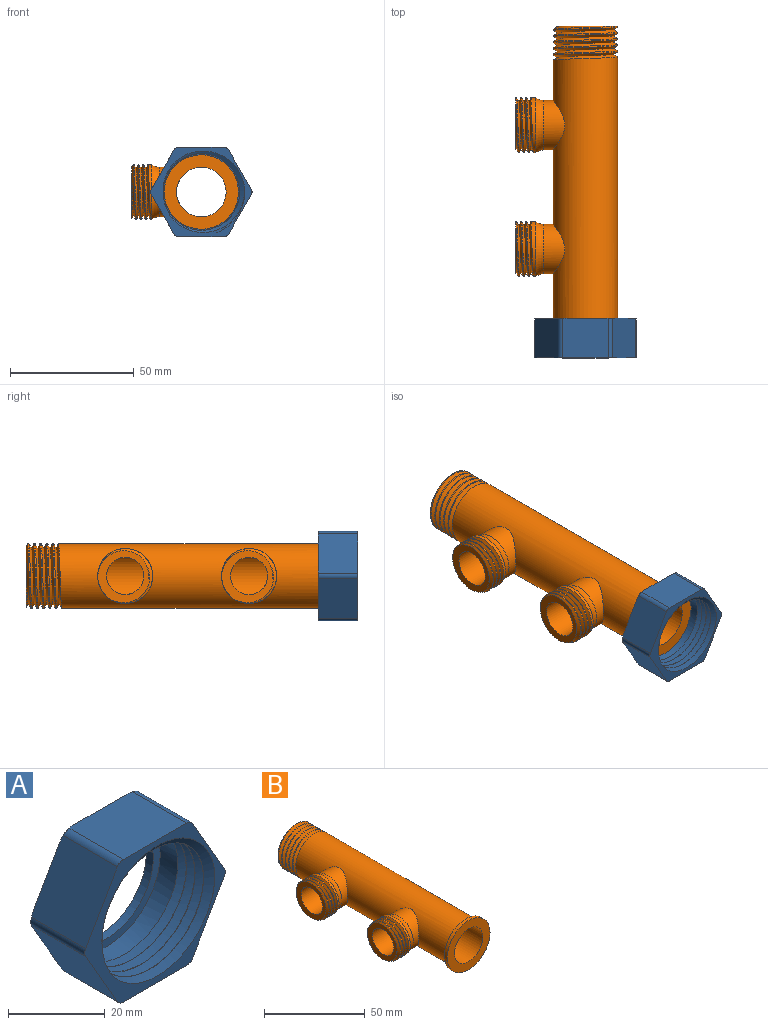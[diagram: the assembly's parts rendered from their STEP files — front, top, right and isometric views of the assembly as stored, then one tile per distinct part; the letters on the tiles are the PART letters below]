
ASSEMBLY  parts=2 mates=1
PART A: 29 faces, bbox 43.9x19.3x42.2 mm
  f0: cylinder r=15.45mm len=30.9mm, axis (0,1,0), area 510.3mm2, adj f3,f10,f26,f27,f28
  f1: cylinder r=15.45mm len=19.43mm, axis (0,1,0), area 2.6mm2, adj f2,f4,f27,f28
  f2: cylinder r=15.45mm len=30.9mm, axis (0,1,0), area 9.7mm2, adj f1,f3,f27,f28
  f3: cylinder r=15.45mm len=30.9mm, axis (0,1,0), area 9.7mm2, adj f0,f2,f27,f28
  f4: plane 42.7x37.75mm, normal (0,-1,0), area 270mm2, adj f1,f14,f15,f16,f17,f18,f19,f20
  f5: torus R=19.45mm, axis (0,1,0), area 3.3mm2, adj f12,f14,f15,f20
  f6: torus R=19.45mm, axis (0,1,0), area 3.3mm2, adj f12,f15,f16,f21
  f7: torus R=19.45mm, axis (0,1,0), area 3.3mm2, adj f12,f16,f17,f22
  f8: torus R=19.45mm, axis (0,1,0), area 3.3mm2, adj f12,f17,f18,f23
  f9: torus R=19.45mm, axis (0,1,0), area 3.3mm2, adj f12,f14,f19,f25
  f10: plane 30.9x30.9mm, normal (0,-1,0), area 179.6mm2, adj f0,f13
  f11: torus R=19.45mm, axis (0,1,0), area 3.3mm2, adj f12,f18,f19,f24
  f12: plane 38.9x36mm, normal (0,1,0), area 532mm2, adj f5,f6,f7,f8,f9,f11,f13,f14
  f13: cylinder r=13.47mm len=26.95mm, axis (0,1,0), area 175.1mm2, adj f10,f12
  f14: plane 16.07x16.07mm, normal (-0.87,0,-0.5), area 295.4mm2, adj f4,f5,f9,f12,f20,f25
  f15: plane 16.07x16.07mm, normal (-0.87,0,0.5), area 295.4mm2, adj f4,f5,f6,f12,f20,f21
  f16: plane 18.54x16.07mm, normal (0,0,1), area 295.4mm2, adj f4,f6,f7,f12,f21,f22
  f17: plane 16.07x16.07mm, normal (0.87,0,0.5), area 295.4mm2, adj f4,f7,f8,f12,f22,f23
  f18: plane 16.07x16.07mm, normal (0.87,0,-0.5), area 295.4mm2, adj f4,f8,f11,f12,f23,f24
  f19: plane 18.54x16.07mm, normal (0,0,-1), area 295.4mm2, adj f4,f9,f11,f12,f24,f25
  f20: cylinder r=2mm len=15.84mm, axis (0,-1,0), area 33.2mm2, adj f4,f5,f14,f15
  f21: cylinder r=2mm len=15.84mm, axis (0,-1,0), area 33.2mm2, adj f4,f6,f15,f16
  f22: cylinder r=2mm len=15.84mm, axis (0,-1,0), area 33.2mm2, adj f4,f7,f16,f17
  f23: cylinder r=2mm len=15.84mm, axis (0,-1,0), area 33.2mm2, adj f4,f8,f17,f18
  f24: cylinder r=2mm len=15.84mm, axis (0,-1,0), area 33.2mm2, adj f4,f11,f18,f19
  f25: cylinder r=2mm len=15.84mm, axis (0,-1,0), area 33.2mm2, adj f4,f9,f14,f19
  f26: plane 2.4x2.08mm, normal (0,0,-1), area 2.5mm2, adj f0,f27,f28
  f27: bspline ~40.48x35.06mm, area 934.5mm2, adj f0,f1,f2,f3,f4,f26,f28
  f28: bspline ~40.48x35.06mm, area 817.6mm2, adj f0,f1,f2,f3,f4,f26,f27
PART B: 31 faces, bbox 45.2x124.3x31.2 mm
  f0: cylinder r=10mm len=122mm, axis (0,1,0), area 7279.5mm2, adj f8,f16,f24,f26
  f1: cylinder r=13mm len=107.5mm, axis (0,1,0), area 7987.8mm2, adj f7,f15,f23,f27,f29,f30
  f2: cylinder r=13mm len=12.4mm, axis (0,1,0), area 4.1mm2, adj f3,f8,f28
  f3: cylinder r=13mm len=26mm, axis (0,1,0), area 40.9mm2, adj f2,f4,f28,f29
  f4: cylinder r=13mm len=26mm, axis (0,1,0), area 40.8mm2, adj f3,f5,f28,f29
  f5: cylinder r=13mm len=26mm, axis (0,1,0), area 40.9mm2, adj f4,f6,f28,f29
  f6: cylinder r=13mm len=26mm, axis (0,1,0), area 40.8mm2, adj f5,f7,f28,f29
  f7: cylinder r=13mm len=26mm, axis (0,1,0), area 40.7mm2, adj f1,f6,f28,f29
  f8: plane 25.89x25.86mm, normal (0,1,0), area 162.7mm2, adj f0,f2,f28,f29
  f9: bspline ~25.58x22.15mm, area 370.2mm2, adj f10,f11,f13,f14
  f10: bspline ~25.58x22.15mm, area 419.4mm2, adj f9,f11,f13,f14
  f11: plane 1.7x1.47mm, normal (0,0,-1), area 1.3mm2, adj f9,f10,f14
  f12: torus R=15mm, axis (-1,0,0), area 217.5mm2, adj f14,f15
  f13: plane 21.98x21.95mm, normal (-1,0,0), area 167.1mm2, adj f9,f10,f14,f16
  f14: cylinder r=11.07mm len=22.15mm, axis (1,0,0), area 138.7mm2, adj f9,f10,f11,f12,f13
  f15: cylinder r=10mm len=20mm, axis (1,0,0), area 384.5mm2, adj f1,f12
  f16: cylinder r=7.5mm len=21.39mm, axis (-1,0,0), area 1007.8mm2, adj f0,f13
  f17: bspline ~25.58x22.15mm, area 370.2mm2, adj f18,f19,f21,f22
  f18: bspline ~25.58x22.15mm, area 419.4mm2, adj f17,f19,f21,f22
  f19: plane 1.7x1.47mm, normal (0,0,-1), area 1.3mm2, adj f17,f18,f22
  f20: torus R=15mm, axis (-1,0,0), area 217.5mm2, adj f22,f23
  f21: plane 21.98x21.95mm, normal (-1,0,0), area 167.1mm2, adj f17,f18,f22,f24
  f22: cylinder r=11.07mm len=22.15mm, axis (1,0,0), area 138.7mm2, adj f17,f18,f19,f20,f21
  f23: cylinder r=10mm len=20mm, axis (1,0,0), area 384.5mm2, adj f1,f20
  f24: cylinder r=7.5mm len=21.39mm, axis (1,0,0), area 1007.8mm2, adj f0,f21
  f25: cylinder r=15mm len=30mm, axis (0,1,0), area 188.5mm2, adj f26,f27
  f26: plane 30x30mm, normal (0,-1,0), area 392.7mm2, adj f0,f25
  f27: plane 30x30mm, normal (0,1,0), area 175.9mm2, adj f1,f25
  f28: bspline ~30.02x26mm, area 822.9mm2, adj f2,f3,f4,f5,f6,f7,f8,f29
  f29: bspline ~30.02x26mm, area 885.4mm2, adj f1,f3,f4,f5,f6,f7,f8,f28
  f30: plane 2x1.73mm, normal (0,0,-1), area 1.7mm2, adj f1,f28,f29
PLACE A t=(-97.66,46.01,11.13)mm
PLACE B t=(-97.66,-13.07,11.13)mm
MATE revolute A.f0 <-> B.f0  axis (0,-1,0) through (-97.66,-133.07,11.13)mm
